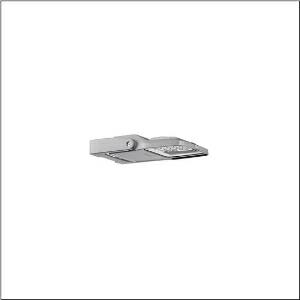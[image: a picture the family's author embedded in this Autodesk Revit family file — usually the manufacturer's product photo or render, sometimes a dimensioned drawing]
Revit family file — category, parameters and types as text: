
# Revit family: floodlight_fl_21_iq_micro___pl43_5xa7762a4a2a_306a
name_source: partatom
category: Lighting Fixtures
units: mm (PartAtom-declared; Revit-internal decimal feet)

## family parameters
Cut with Voids When Loaded = No
Host = Face
Light Source = No
Part Type = Normal
Room Calculation Point = No
Round Connector Dimension = Use Diameter
Shared = No

## types (1)
- --- (1 x LED, 3170 lm, 23.1 W, 4000K)
    Apparent Load = 23 VA
    CIE Flux Codes = 29 80 99 100 100
    Color Rendering = 70
    Color Temperature = 4000K
    Default Elevation = 1800 mm
    Description = Floodlight FL 21 iQ micro, floodlight, primary light control with lens, of PMMA, primary optical cover: protective disc, of toughened safety glass, transparent, light distribution: PL43, light emission: direct distribution, installation type: surface-mounted, lamps: LED, High Power LED, rated values: 3.170lm | 23,1W | 137,2lm/W (begin service life); end service life: 3.170lm | 23,8W; at 50% lumin. flux: 1.585lm | 11W | 144,1lm/W, colour temperature: 4000K, colour rendering: CRI > 70, light colour: 740, light setting 1 begin service life: 100% | 3.170lm | 23,1W | 137,2lm/W | 4.000K, light setting 1 end service life: 23,8W, further light settings possible, control: Auto-Match, Temp-Guard, Night-Set, Smart-Wire, Desk-Remote (wireless, voltage-free reading and setting of iQ features in the workshop via application-optimized NFC function/RFID function), optimised constant luminous flux control (CLO 2.0), Street-Remote, pre-setting: linear dimming characteristic, with terminal, 6-pole, mains connection: 220..240V, AC, 50/60Hz, luminaire housing, of diecast aluminium, powder-coated, SITECO metallic grey (DB 702S), corrosivity category C5 mid according to DIN EN ISO 12944suitable for swimming poolschlorine-resistant, sealing non-destructively replaceable, design bracket, of diecast aluminium, powder-coated, SITECO metallic grey (DB 702S), protection rating (complete): IP66, insulation class (complete): insulation class II (safety insulation), certification: CE, ENEC, VDE, protection symbol: D, impact resistance: IK07, permissible operating ambient temperature: -40..+40°C, permissible operating ambient temperature for outdoor applications: -40..+50°C, standard: DIN EN 12944, LABS conformity tested according to VDMA 24364:2018-05, packaging unit: 1 piece

Light Distribution: PL43
    Height = 65 mm
    Lamp = 1 x LED
    Lamp Light Flux = 3170 lm
    Lamp Power = 23.1 W
    Lamp count = 1
    Length = 312 mm
    Luminous efficacy = 137 lm/W
    Manufacturer = Siteco
    ModVariant = No
    Model = 5XA7762A4A2A
    Mounting Place = Wall
    Mounting Type = Surface mounted
    Number of Poles = 1
    OnlyDefault = Yes
    Power Factor = 1
    Product Name = Floodlight FL 21 iQ micro | PL43
    Product group = floodlight | wall mounted
    ProductGroupID = 2002
    Protection Class = Protection class II
    Protection Degree = IP 66
    RLX_Detail_Level = 1
    RLX_Emergency_Light_Flux = 0 lm
    RLX_Emergency_Type = 0
    RLX_Emergency_Type_DB = No
    RlxData = <blob elided: 97433 chars, md5=5b2859d8>
    Socket = socket
    Standby Power = 0 W
    System Light Flux = 3170 lm
    System Power = 23 W
    Type Comments = factory setting: luminous flux: 100 % | dim-lin: 254 | 455 mA
    Type Image = l_1006878.jpg
    URL = http://relux.com
    VarID = @adj_175989
    Voltage = 0 V
    Weight = 0.00 kg
    Width = 230 mm

## geometry (parser evidence)
native form markers: Blend x4, Sweep x13
no freeform markers — native parametric forms only
